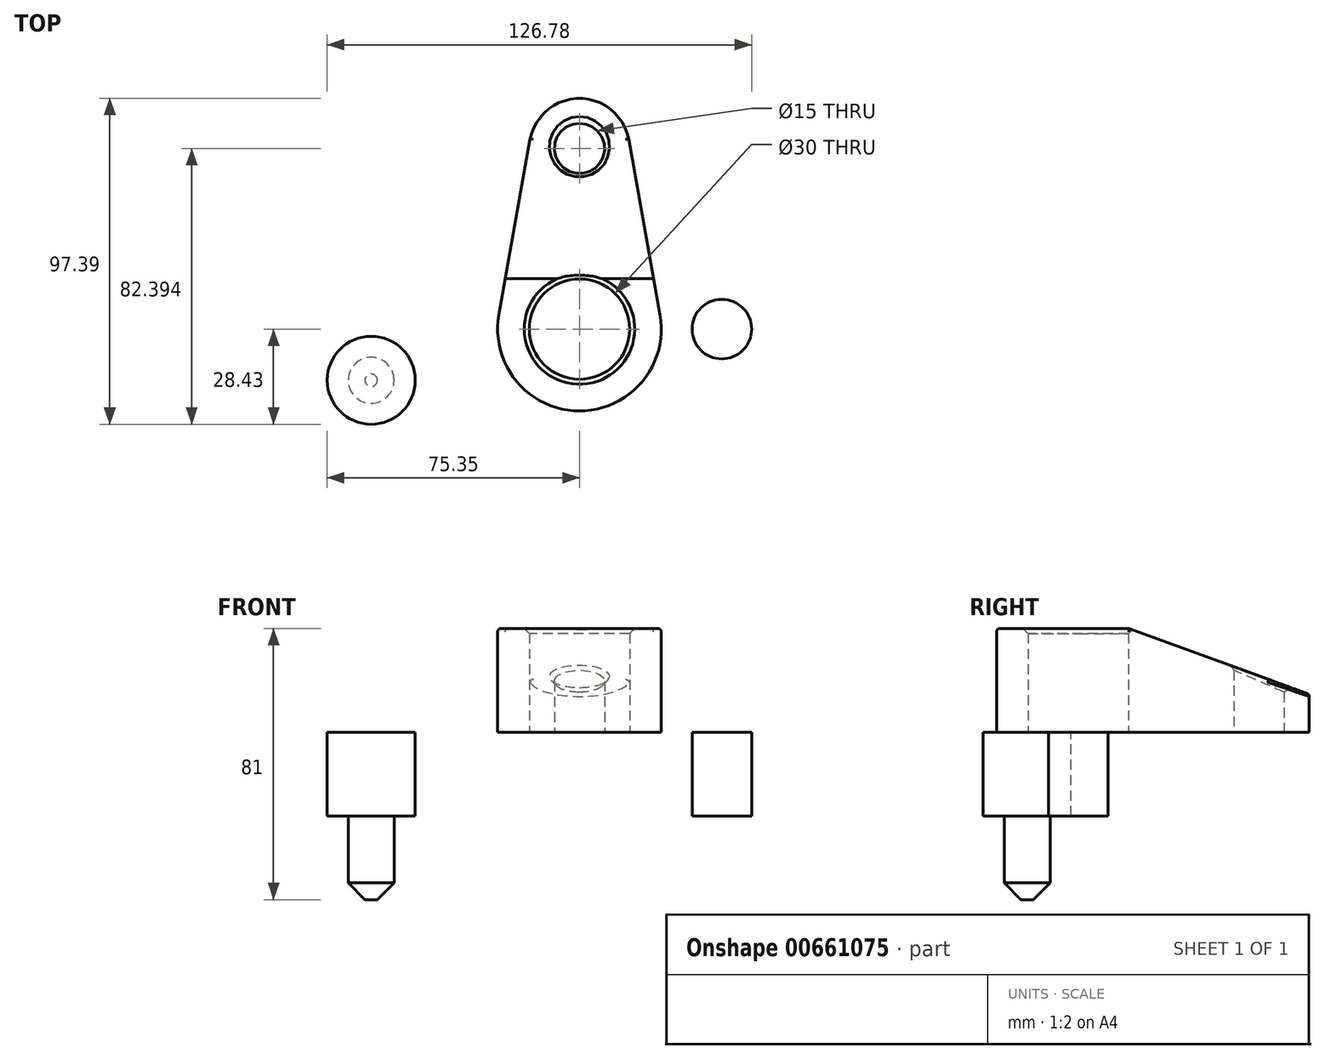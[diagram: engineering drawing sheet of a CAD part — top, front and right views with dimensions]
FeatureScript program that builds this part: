
annotation { "Feature Type Name" : "Feature", "Feature Type Description" : "" }
export const myFeature = defineFeature(function(context is Context, id is Id, definition is map)
    precondition{}
    {
        {
            var Q0;
            Q0=qCreatedBy(makeId("Top.planeOp"),FACE);
            var sketch = newSketch(context, id + "F0", { "sketchPlane" : qUnion([Q0])});
            skCircle(sketch, "E0", {"center": v(0, 0) * mm, "radius": 24.44 * mm});
            skCircle(sketch, "E1", {"center": v(0, 0) * mm, "radius": 15 * mm});
            skCircle(sketch, "E2", {"center": v(0, 53.96) * mm, "radius": 15 * mm});
            skCircle(sketch, "E3", {"center": v(0, 53.96) * mm, "radius": 7.5 * mm});
            skLineSegment(sketch, "E4", {"start": v(-14.77, 56.59) * mm, "end": v(-24.07, 4.28) * mm});
            skLineSegment(sketch, "E5", {"start": v(14.77, 56.59) * mm, "end": v(24.07, 4.28) * mm});
            skSolve(sketch);
        }
        {
            var Q0;
            {var subQ0=sQuery(id+"F0.wireOp",EDGE,"E4");Q0=makeQuery(id+"F0.imprint","IMPRINT",FACE,{"disambiguationData":[TD([[makeQuery(id+"F0.imprint","IMPRINT",EDGE,{"derivedFrom":subQ0}),1.0]])]});}
            var Q1;
            Q1=makeQuery(id+"F0.imprint","IMPRINT",FACE,{"disambiguationData":[TD([[makeQuery(id+"F0.imprint","IMPRINT",EDGE,{"derivedFrom":sQuery(id+"F0.wireOp",EDGE,"E1")}),-1.0]])]});
            var Q2;
            Q2=makeQuery(id+"F0.imprint","IMPRINT",FACE,{"disambiguationData":[TD([[makeQuery(id+"F0.imprint","IMPRINT",EDGE,{"derivedFrom":sQuery(id+"F0.wireOp",EDGE,"E3")}),-1.0]])]});
            extrude(context, id + "F1", {"entities" : qUnion([Q0, Q1, Q2]), "depth" : 31 * mm, "offsetDistance" : 25 * mm});
        }
        {
            var Q0;
            Q0=qCreatedBy(makeId("Top.planeOp"),FACE);
            var sketch = newSketch(context, id + "F2", { "sketchPlane" : qUnion([Q0])});
            skCircle(sketch, "E6", {"center": v(-62.21, -15.3) * mm, "radius": 13.13 * mm});
            skSolve(sketch);
        }
        {
            var Q0;
            Q0=makeQuery(id+"F2.imprint","IMPRINT",FACE,{"disambiguationData":[TD([[makeQuery(id+"F2.imprint","IMPRINT",EDGE,{"derivedFrom":sQuery(id+"F2.wireOp",EDGE,"E6")}),1.0]])]});
            extrude(context, id + "F3", {"entities" : qUnion([Q0]), "depth" : 25 * mm, "offsetDistance" : 25 * mm});
        }
        {
            var Q0;
            Q0=makeQuery(id+"F3.opExtrude","CAP_FACE",FACE,{"disambiguationData":[OSD([sQuery(id+"F2.wireOp",EDGE,"E6")])],"isStart":false});
            var sketch = newSketch(context, id + "F4", { "sketchPlane" : qUnion([Q0])});
            skCircle(sketch, "E7", {"center": v(-62.21, -15.3) * mm, "radius": 6.86 * mm});
            skSolve(sketch);
        }
        {
            var Q0;
            Q0 = qSketchRegion(id + "F4", true);
            extrude(context, id + "F5", {"entities" : qUnion([Q0]), "operationType" : NewBodyOperationType.ADD, "depth" : 25 * mm, "offsetDistance" : 25 * mm});
        }
        {
            var Q0;
            Q0=makeQuery(id+"F5.opExtrude","CAP_EDGE",EDGE,{"disambiguationData":[OSD([sQuery(id+"F4.wireOp",EDGE,"E7")])],"isStart":false});
            chamfer(context, id + "F6", {"entities" : qUnion([Q0]), "width" : 5 * mm, "tangentPropagation" : true});
        }
        {
            var Q0;
            Q0=makeQuery(id+"F3.opExtrude","SWEPT_BODY",BODY,{"disambiguationData":[OSD([sQuery(id+"F2.wireOp",EDGE,"E6")])]});
            var Q1;
            Q1=qCreatedBy(makeId("Top.planeOp"),FACE);
            mirror(context, id + "F7", {"entities" : qUnion([Q0]), "mirrorPlane" : qUnion([Q1])});
        }
        {
            var Q0;
            Q0=qCreatedBy(makeId("Top.planeOp"),FACE);
            var sketch = newSketch(context, id + "F8", { "sketchPlane" : qUnion([Q0])});
            skCircle(sketch, "E8", {"center": v(42.53, 0) * mm, "radius": 8.9 * mm});
            skSolve(sketch);
        }
        {
            var Q0;
            Q0=makeQuery(id+"F8.imprint","IMPRINT",FACE,{"disambiguationData":[TD([[makeQuery(id+"F8.imprint","IMPRINT",EDGE,{"derivedFrom":sQuery(id+"F8.wireOp",EDGE,"E8")}),1.0]])]});
            extrude(context, id + "F9", {"entities" : qUnion([Q0]), "depth" : 25 * mm, "offsetDistance" : 25 * mm});
        }
        {
            var Q0;
            Q0=makeQuery(id+"F9.opExtrude","SWEPT_BODY",BODY,{"disambiguationData":[OSD([sQuery(id+"F8.wireOp",EDGE,"E8")])]});
            var Q1;
            Q1=qCreatedBy(makeId("Top.planeOp"),FACE);
            mirror(context, id + "F10", {"entities" : qUnion([Q0]), "mirrorPlane" : qUnion([Q1])});
        }
        {
            var Q0;
            Q0=qCreatedBy(makeId("Right.planeOp"),FACE);
            var sketch = newSketch(context, id + "F11", { "sketchPlane" : qUnion([Q0])});
            skLineSegment(sketch, "E9", {"start": v(0, 0) * mm, "end": v(0, 31.02) * mm, "construction": true});
            skLineSegment(sketch, "E10", {"start": v(15, 31.02) * mm, "end": v(83.5, 31.02) * mm});
            skLineSegment(sketch, "E11", {"start": v(83.5, 31.02) * mm, "end": v(83.5, 6.09) * mm});
            skLineSegment(sketch, "E12", {"start": v(83.5, 6.09) * mm, "end": v(15, 31.02) * mm});
            skSolve(sketch);
        }
        {
            var Q0;
            Q0=makeQuery(id+"F11.imprint","IMPRINT",FACE,{"disambiguationData":[TD([[makeQuery(id+"F11.imprint","IMPRINT",EDGE,{"derivedFrom":sQuery(id+"F11.wireOp",EDGE,"E10")}),-1.0]])]});
            extrude(context, id + "F12", {"entities" : qUnion([Q0]), "operationType" : NewBodyOperationType.REMOVE, "endBound" : BoundingType.SYMMETRIC, "oppositeDirection" : true, "depth" : 46.2 * mm, "offsetDistance" : 25 * mm});
        }
        {
            var Q0;
            Q0=makeQuery(id+"F12.boolean.opBoolean","INTERSECT",EDGE,{"derivedFrom":[makeQuery(id+"F1.opExtrude","SWEPT_FACE",FACE,{"disambiguationData":[OSD([sQuery(id+"F0.wireOp",EDGE,"E5")])]}),makeQuery(id+"F12.opExtrude","SWEPT_FACE",FACE,{"disambiguationData":[OSD([sQuery(id+"F11.wireOp",EDGE,"E12")])]})]});
            var Q1;
            Q1=makeQuery(id+"F1.opExtrude","CAP_EDGE",EDGE,{"disambiguationData":[OSD([sQuery(id+"F0.wireOp",EDGE,"E5")])],"isStart":false});
            var Q2;
            Q2=makeQuery(id+"F1.opExtrude","CAP_EDGE",EDGE,{"disambiguationData":[OSD([sQuery(id+"F0.wireOp",EDGE,"E0")])],"isStart":false});
            var Q3;
            Q3=makeQuery(id+"F1.opExtrude","CAP_EDGE",EDGE,{"disambiguationData":[OSD([sQuery(id+"F0.wireOp",EDGE,"E4")])],"isStart":false});
            var Q4;
            Q4=makeQuery(id+"F12.boolean.opBoolean","INTERSECT",EDGE,{"derivedFrom":[makeQuery(id+"F1.opExtrude","SWEPT_FACE",FACE,{"disambiguationData":[OSD([sQuery(id+"F0.wireOp",EDGE,"E4")])]}),makeQuery(id+"F12.opExtrude","SWEPT_FACE",FACE,{"disambiguationData":[OSD([sQuery(id+"F11.wireOp",EDGE,"E12")])]})]});
            var Q5;
            Q5=makeQuery(id+"F12.boolean.opBoolean","INTERSECT",EDGE,{"derivedFrom":[makeQuery(id+"F1.opExtrude","SWEPT_FACE",FACE,{"disambiguationData":[OSD([sQuery(id+"F0.wireOp",EDGE,"E2")])]}),makeQuery(id+"F12.opExtrude","SWEPT_FACE",FACE,{"disambiguationData":[OSD([sQuery(id+"F11.wireOp",EDGE,"E12")])]})]});
            fillet(context, id + "F13", {"entities" : qUnion([Q0, Q1, Q2, Q3, Q4, Q5]), "radius" : 1 * mm, "tangentPropagation" : true, "allowEdgeOverflow" : false});
        }
        {
            var Q0;
            Q0=makeQuery(id+"F1.opExtrude","CAP_EDGE",EDGE,{"disambiguationData":[OSD([sQuery(id+"F0.wireOp",EDGE,"E1")])],"isStart":false});
            var Q1;
            Q1=makeQuery(id+"F12.boolean.opBoolean","INTERSECT",EDGE,{"derivedFrom":[makeQuery(id+"F1.opExtrude","SWEPT_FACE",FACE,{"disambiguationData":[OSD([sQuery(id+"F0.wireOp",EDGE,"E3")])]}),makeQuery(id+"F12.opExtrude","SWEPT_FACE",FACE,{"disambiguationData":[OSD([sQuery(id+"F11.wireOp",EDGE,"E12")])]})]});
            chamfer(context, id + "F14", {"entities" : qUnion([Q0, Q1]), "width" : 1.5 * mm, "tangentPropagation" : true});
        }
        {
            var Q0;
            Q0=makeQuery(id+"F9.opExtrude","SWEPT_BODY",BODY,{"disambiguationData":[OSD([sQuery(id+"F8.wireOp",EDGE,"E8")])]});
            deleteBodies(context, id + "F15", {"entities" : qUnion([Q0])});
        }
        {
            var Q0;
            Q0=makeQuery(id+"F3.opExtrude","SWEPT_BODY",BODY,{"disambiguationData":[OSD([sQuery(id+"F2.wireOp",EDGE,"E6")])]});
            deleteBodies(context, id + "F16", {"entities" : qUnion([Q0])});
        }
    });
